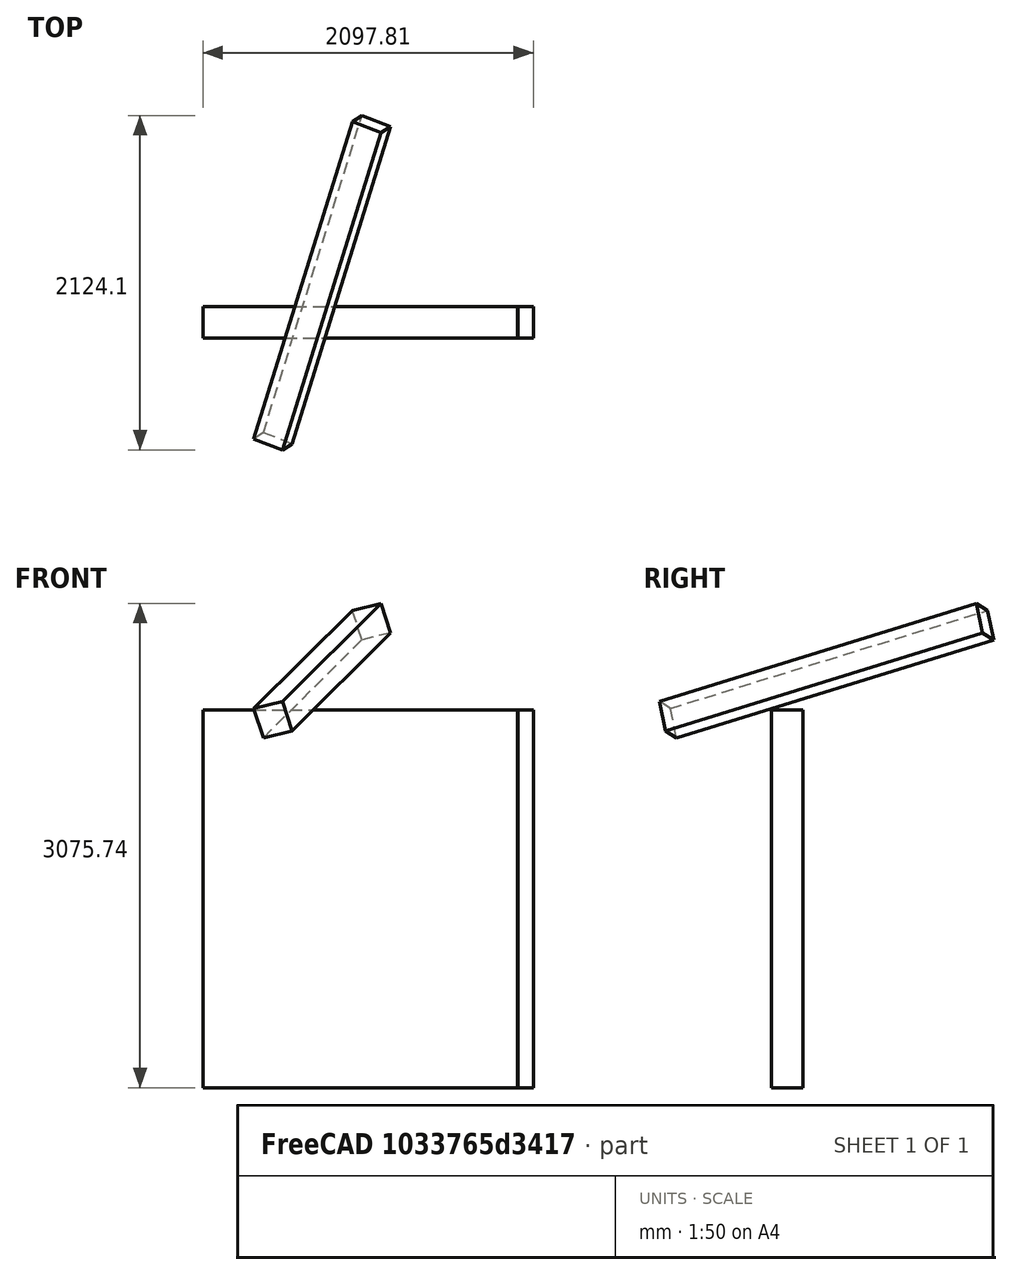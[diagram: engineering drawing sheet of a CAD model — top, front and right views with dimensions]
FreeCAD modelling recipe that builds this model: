
FCSTD DOCUMENT  (FreeCAD 0.20R29603 (Git))
Label: arch-workbench-tutorial
License: All rights reserved
LicenseURL: http://en.wikipedia.org/wiki/All_rights_reserved
objects: Part::FeaturePython×4, Sketcher::SketchObject×1
note: 5 computed .brp shape members not serialized (recipe doc carries the construction recipe); baked Part::Feature solids carry a one-line shape summary decoded from their .brp

FEATURE [Sketcher::SketchObject] WallTrace
  FullyConstrained = false
  sketch-geometry (1):
    g0: LineSegment StartX=-1268.12 StartY=112.865 StartZ=0 EndX=731.876 EndY=112.865 EndZ=0
FEATURE [Part::FeaturePython] Wall  # Arch/BIM 166 (typed FeaturePython)
  Align = 2
  Area = 4800000
  Base = -> WallTrace
  BlockHeight = 0
  BlockLength = 0
  CountBroken = 0
  CountEntire = 0
  Face = 0
  Height = 2400
  HorizontalArea = 400000
  IfcData = attributes={"GlobalId": {"name": "GlobalId", "type": "IfcGloballyUniqueId", "is_enum": false, "enum_values": []}, "Description": {"... (+533 chars omitted),+1 more (map truncated)
  IfcType = 166
  Joint = 0
  Length = 2000
  MakeBlocks = false
  MoveBase = false
  MoveWithHost = false
  Normal = (0,0,1)
  OffsetFirst = 0
  OffsetSecond = 0
  PerimeterLength = 4400
  PredefinedType = 0
  VerticalArea = 1.056e+07
  Width = 200
FEATURE [Part::FeaturePython] Structure  # Arch/BIM 172 (typed FeaturePython)
  Base = -> Wall
  BaseMirror = false
  BaseOffsetX = 0
  BaseOffsetY = 0
  BasePerpendicularToTool = false
  BaseRotation = 0
  ComputedLength = 2400
  FaceMaker = 0
  Height = 1000
  HorizontalArea = 400000
  IfcData = attributes={"GlobalId": {"name": "GlobalId", "type": "IfcGloballyUniqueId", "is_enum": false, "enum_values": []}, "Description": {"... (+484 chars omitted),+1 more (map truncated)
  IfcType = 172
  Length = 0
  MoveBase = false
  MoveWithHost = false
  Nodes = (2) [(-268.124,112.865,0),(-268.124,112.865,2400)]
  NodesOffset = 0
  Normal = (0,0,0)
  PerimeterLength = 4400
  Placement = pos=(0.0100897,0.00865248,0.00416759) rot=(0,0,1;0rad)
  PredefinedType = 0
  ToolOffsetFirst = 0
  ToolOffsetLast = 0
  VerticalArea = 1.056e+07
  Width = 100
FEATURE [Part::FeaturePython] Structure001  label="Column"  # Arch/BIM 24 (typed FeaturePython)
  BaseMirror = false
  BaseOffsetX = 0
  BaseOffsetY = 0
  BasePerpendicularToTool = false
  BaseRotation = 0
  ComputedLength = 2400
  FaceMaker = 0
  Height = 2400
  HorizontalArea = 20000
  IfcData = attributes={"GlobalId": {"name": "GlobalId", "type": "IfcGloballyUniqueId", "is_enum": false, "enum_values": []}, "Description": {"... (+438 chars omitted),+1 more (map truncated)
  IfcType = 24
  Length = 100
  MoveBase = false
  MoveWithHost = false
  Nodes = (2) [(-3.88578e-16,0,0),(-3.88578e-16,0,2400)]
  NodesOffset = 0
  Normal = (0,0,0)
  PerimeterLength = 600
  Placement = pos=(779.7,112.9,0) rot=(0,0,1;0rad)
  PredefinedType = 0
  ToolOffsetFirst = 0
  ToolOffsetLast = 0
  VerticalArea = 1440000
  Width = 200
FEATURE [Part::FeaturePython] Structure002  label="Beam"  # Arch/BIM 7 (typed FeaturePython)
  BaseMirror = false
  BaseOffsetX = 0
  BaseOffsetY = 0
  BasePerpendicularToTool = false
  BaseRotation = 0
  ComputedLength = 2200
  FaceMaker = 0
  Height = 200
  HorizontalArea = 666627
  IfcData = attributes={"GlobalId": {"name": "GlobalId", "type": "IfcGloballyUniqueId", "is_enum": false, "enum_values": []}, "Description": {"... (+475 chars omitted),+1 more (map truncated)
  IfcType = 7
  Length = 2200
  MoveBase = false
  MoveWithHost = false
  Nodes = (2) [(4.31408e-32,0,-7.77156e-16),(2200,0,-7.77156e-16)]
  NodesOffset = 0
  Normal = (0,0,0)
  PerimeterLength = 0
  Placement = pos=(-824.561,-644.615,2337.95) rot=(0.683521,0.333279,0.649403;1.92039rad)
  PredefinedType = 0
  ToolOffsetFirst = 0
  ToolOffsetLast = 0
  VerticalArea = 0
  Width = 200
